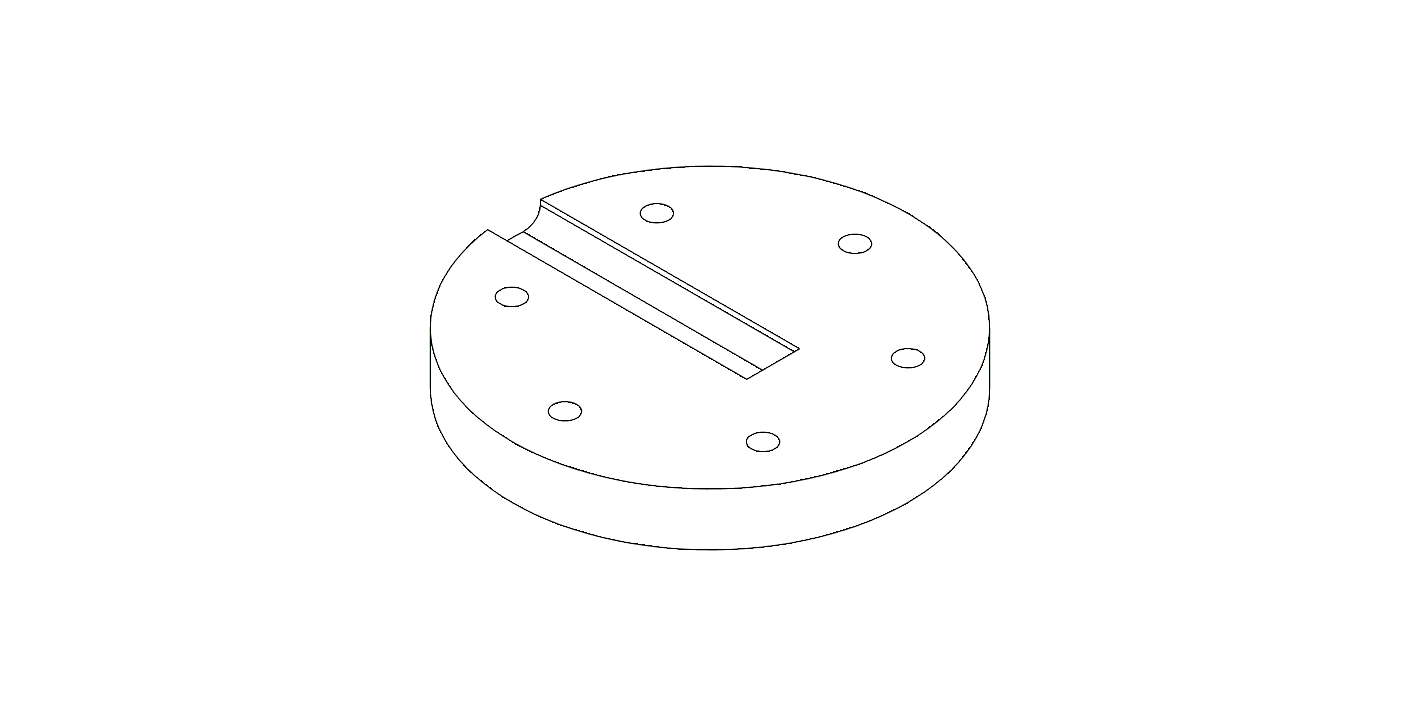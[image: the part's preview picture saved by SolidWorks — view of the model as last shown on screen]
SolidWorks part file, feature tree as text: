
SOLIDWORKS PART (.sldprt)
format: sldprt  version: not decoded by parser v0  size: 204,800 bytes
history: native  units: mm
features: sketch x2, material x1, extrude x1, cut_extrude x1, fillet x1 (+13 scaffold rows collapsed)
feature tree (19):
  scaffold x13  (default folders/planes/origin — collapsed)
  material  "Material <not specified>"
  sketch  "Sketch1"  dims[c1.D1=75.0mm c1.D2=4.5mm c1.D3=4.2mm c1.D5=4.2mm c2.D3=27.5mm c2.D4=27.5mm c2.D5=13.75mm c2.D6=~23.815699mm c2.D7=~23.815699mm c3.D7=60.0deg c3.D4=6.0]
  extrude  "Boss-Extrude1"  Depth=10mm
  sketch  "Sketch2"  dims[c1.D1=~34.38746mm c2.D1=27.5deg c2.D2=~26.717199mm c3.D2=27.5deg c3.D3=~18.706872mm c4.D3=90.0deg c4.D4=~33.262906mm c5.D4=90.0deg c6.D4=5.0mm c6.D5=5.0mm c6.D6=5.0mm c6.D7=~24.38805mm c6.D8=12.0mm c6.D1=~14.277392mm c7.D1=90.0deg c7.D2=5.0mm c7.D3=5.0mm c7.D4=12.0mm c7.D5=10.0mm]
  cut_extrude  "Cut-Extrude1"  Depth=4mm
  fillet  "Fillet1"  Radius=3mm
decode coverage: 5 of 5 modeling features carry decoded parameters
note: ~ marks probable driven/reference dimensions
note: suppression state not decoded; provenance and decode notes live in map.json
